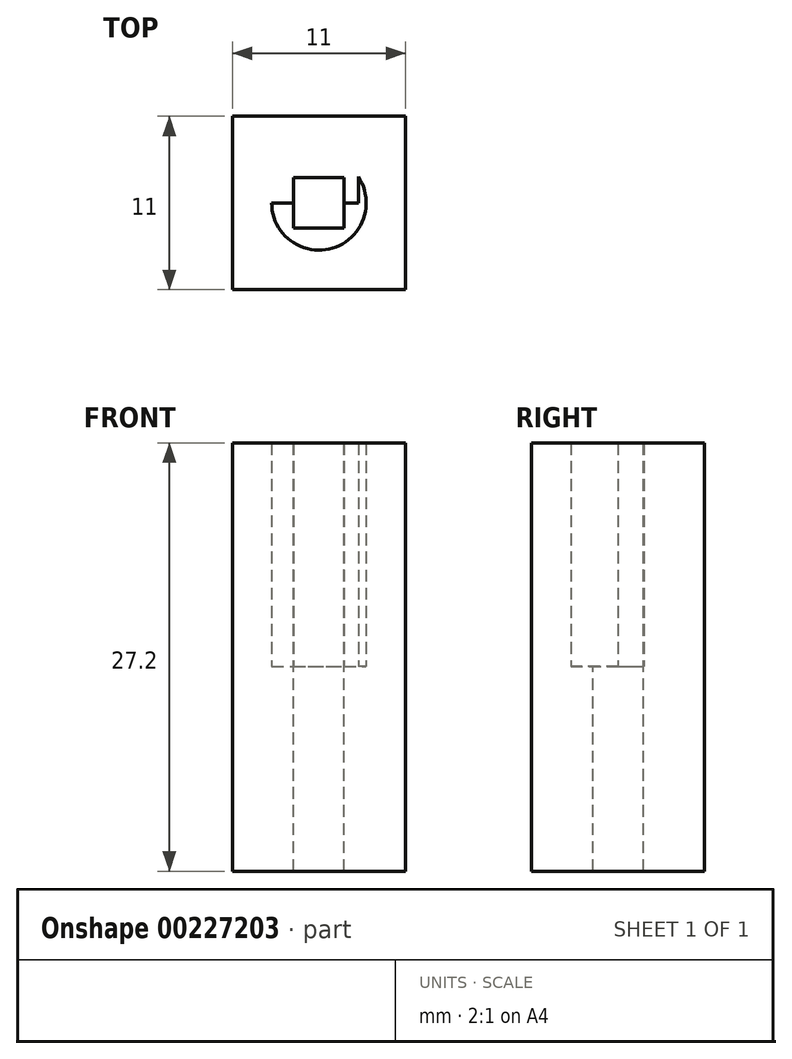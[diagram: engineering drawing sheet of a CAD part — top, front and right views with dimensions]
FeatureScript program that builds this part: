
annotation { "Feature Type Name" : "Feature", "Feature Type Description" : "" }
export const myFeature = defineFeature(function(context is Context, id is Id, definition is map)
    precondition{}
    {
        {
            var Q0;
            Q0=qCreatedBy(makeId("Top.planeOp"),FACE);
            var sketch = newSketch(context, id + "F0", { "sketchPlane" : qUnion([Q0])});
            skCircle(sketch, "E0", {"center": v(0, 0) * mm, "radius": 3 * mm});
            skLineSegment(sketch, "E1", {"start": v(-3, 0) * mm, "end": v(2.5, 0) * mm});
            skLineSegment(sketch, "E2", {"start": v(2.5, -1.66) * mm, "end": v(2.5, 1.66) * mm});
            skLineSegment(sketch, "E3.bottom", {"start": v(5.5, 5.5) * mm, "end": v(-5.5, 5.5) * mm});
            skLineSegment(sketch, "E3.top", {"start": v(5.5, -5.5) * mm, "end": v(-5.5, -5.5) * mm});
            skLineSegment(sketch, "E3.left", {"start": v(5.5, 5.5) * mm, "end": v(5.5, -5.5) * mm});
            skLineSegment(sketch, "E3.right", {"start": v(-5.5, 5.5) * mm, "end": v(-5.5, -5.5) * mm});
            skSolve(sketch);
        }
        {
            var Q0;
            Q0=makeQuery(id+"F0.imprint","IMPRINT",FACE,{"disambiguationData":[TD([[makeQuery(id+"F0.imprint","IMPRINT",EDGE,{"derivedFrom":sQuery(id+"F0.wireOp",EDGE,"ZaWfL3dz-teJq-2qJw-Bn2j-wU9BD7OHoSHv")}),1.0]])]});
            var Q1;
            {var subQ0=sQuery(id+"F0.wireOp",EDGE,"E2");var subQ1=sQuery(id+"F0.wireOp",EDGE,"E0");var subQ2=makeQuery(id+"F0.imprint","INTERSECT",VERTEX,{"disambiguationData":[OD(0.0)],"derivedFrom":[subQ1,subQ0]});Q1=makeQuery(id+"F0.imprint","IMPRINT",FACE,{"disambiguationData":[TD([[makeQuery(id+"F0.imprint","IMPRINT",EDGE,{"disambiguationData":[TD([[subQ2,-1.0]])],"derivedFrom":subQ1}),1.0]])]});}
            var Q2;
            Q2=makeQuery(id+"F0.imprint","IMPRINT",FACE,{"disambiguationData":[TD([[makeQuery(id+"F0.imprint","IMPRINT",EDGE,{"derivedFrom":sQuery(id+"F0.wireOp",EDGE,"E3.bottom")}),1.0]])]});
            extrude(context, id + "F1", {"entities" : qUnion([Q0, Q1, Q2]), "depth" : 14.2 * mm});
        }
        {
            var Q0;
            Q0=makeQuery(id+"F1.opExtrude","CAP_FACE",FACE,{"disambiguationData":[OSD([sQuery(id+"F0.wireOp",EDGE,"E0"),sQuery(id+"F0.wireOp",EDGE,"E2"),sQuery(id+"F0.wireOp",EDGE,"ZaWfL3dz-teJq-2qJw-Bn2j-wU9BD7OHoSHv")])],"isStart":true});
            var sketch = newSketch(context, id + "F2", { "sketchPlane" : qUnion([Q0])});
            skLineSegment(sketch, "E4.bottom", {"start": v(5.5, -5.5) * mm, "end": v(-5.5, -5.5) * mm});
            skLineSegment(sketch, "E4.top", {"start": v(5.5, 5.5) * mm, "end": v(-5.5, 5.5) * mm});
            skLineSegment(sketch, "E4.left", {"start": v(5.5, -5.5) * mm, "end": v(5.5, 5.5) * mm});
            skLineSegment(sketch, "E4.right", {"start": v(-5.5, -5.5) * mm, "end": v(-5.5, 5.5) * mm});
            skPoint(sketch, "E4.middle", {"position": v(0, 0) * mm});
            skSolve(sketch);
        }
        {
            var Q0;
            Q0=makeQuery(id+"F2.imprint","IMPRINT",FACE,{"disambiguationData":[TD([[makeQuery(id+"F2.imprint","IMPRINT",EDGE,{"derivedFrom":sQuery(id+"F2.wireOp",EDGE,"vzzhTCoM-K7Zn-38xK-Sv41-PlzZ2GA9Vn8e")}),-1.0]])]});
            var Q1;
            Q1=makeQuery(id+"F2.imprint","IMPRINT",FACE,{"disambiguationData":[TD([[makeQuery(id+"F2.imprint","IMPRINT",EDGE,{"derivedFrom":sQuery(id+"F2.wireOp",EDGE,"vzzhTCoM-K7Zn-38xK-Sv41-PlzZ2GA9Vn8e")}),1.0]])]});
            var Q2;
            Q2=makeQuery(id+"F2.imprint","IMPRINT",FACE,{"disambiguationData":[TD([[makeQuery(id+"F2.imprint","IMPRINT",EDGE,{"derivedFrom":makeQuery(id+"F1.opExtrude","CAP_EDGE",EDGE,{"disambiguationData":[OSD([sQuery(id+"F0.wireOp",EDGE,"E0")])],"isStart":true})}),-1.0]])]});
            var Q3;
            Q3=makeQuery(id+"F2.imprint","IMPRINT",FACE,{"disambiguationData":[TD([[makeQuery(id+"F2.imprint","IMPRINT",EDGE,{"derivedFrom":sQuery(id+"F2.wireOp",EDGE,"E4.bottom")}),-1.0]])]});
            extrude(context, id + "F3", {"entities" : qUnion([Q0, Q1, Q2, Q3]), "operationType" : NewBodyOperationType.ADD, "depth" : 3 * mm});
        }
        {
            var Q0;
            Q0=makeQuery(id+"F3.opExtrude","CAP_FACE",FACE,{"disambiguationData":[OSD([sQuery(id+"F2.wireOp",EDGE,"E4.bottom"),sQuery(id+"F2.wireOp",EDGE,"E4.top"),sQuery(id+"F2.wireOp",EDGE,"E4.left"),sQuery(id+"F2.wireOp",EDGE,"E4.right")])],"isStart":false});
            var sketch = newSketch(context, id + "F4", { "sketchPlane" : qUnion([Q0])});
            skLineSegment(sketch, "E5.bottom", {"start": v(-1.6, -1.6) * mm, "end": v(1.6, -1.6) * mm});
            skLineSegment(sketch, "E5.top", {"start": v(-1.6, 1.6) * mm, "end": v(1.6, 1.6) * mm});
            skLineSegment(sketch, "E5.left", {"start": v(-1.6, -1.6) * mm, "end": v(-1.6, 1.6) * mm});
            skLineSegment(sketch, "E5.right", {"start": v(1.6, -1.6) * mm, "end": v(1.6, 1.6) * mm});
            skPoint(sketch, "E5.middle", {"position": v(0, 0) * mm});
            skSolve(sketch);
        }
        {
            var Q0;
            Q0=makeQuery(id+"F4.imprint","IMPRINT",FACE,{"disambiguationData":[TD([[makeQuery(id+"F4.imprint","IMPRINT",EDGE,{"derivedFrom":sQuery(id+"F4.wireOp",EDGE,"E5.bottom")}),-1.0]])]});
            extrude(context, id + "F5", {"entities" : qUnion([Q0]), "operationType" : NewBodyOperationType.ADD, "depth" : 10 * mm});
        }
        {
            var Q0;
            Q0=makeQuery(id+"F3.opExtrude","CAP_FACE",FACE,{"disambiguationData":[OSD([sQuery(id+"F2.wireOp",EDGE,"E4.bottom"),sQuery(id+"F2.wireOp",EDGE,"E4.top"),sQuery(id+"F2.wireOp",EDGE,"E4.left"),sQuery(id+"F2.wireOp",EDGE,"E4.right")])],"isStart":false});
            extrude(context, id + "F6", {"entities" : qUnion([Q0]), "operationType" : NewBodyOperationType.REMOVE, "oppositeDirection" : true, "depth" : 25 * mm});
        }
    });
